# Revit family: Комби-клапан – регулятор расхода 4006_R_SMART_LF_MF
name_source: partatom
category: Rohrzubehör
revit_build: Autodesk Revit 2018 (Build: 20190510_1515(x64)
units: mm (PartAtom-declared; Revit-internal decimal feet)

## family parameters
Arbeitsebenenbasiert = Nein
Beim Laden mit Abzugskörper schneiden = Nein
Bemaßung runder Anschluss = Durchmesser verwenden
Gemeinsam genutzt = Nein
Immer vertikal = Ja
OmniClass-Nummer = 23.65.55.14
OmniClass-Titel = Valves for Liquid Services
Teiletyp = Unterbricht

## types (2) — shared parameters
B01 = 50 mm
B02 = 45.4 mm
B03 = 44.372 mm
B04 = 41.901 mm
B05 = 40.933 mm
B06 = 39.471 mm
B07 = 30.908 mm
B08 = 26 mm
B09 = 7.998 mm  [stored 0.0262402 ft]
E01 = 23 mm  [stored 0.0754593 ft]
E02 = 20.014 mm  [stored 0.0656627 ft]
E03 = 18.385 mm  [stored 0.0603182 ft]
E04 = 19.704 mm  [stored 0.0646457 ft]
E05 = 20.519 mm  [stored 0.0673196 ft]
E06 = 17.921 mm  [stored 0.0587959 ft]
E07 = 5.15 mm
E08 = 20.825 mm  [stored 0.0683235 ft]
E09 = 20.075 mm  [stored 0.0658629 ft]
E10 = 20.427 mm  [stored 0.0670177 ft]
E11 = 10.7 mm  [stored 0.035105 ft]
E12 = 9.001 mm
E13 = 11.063 mm  [stored 0.0362959 ft]
E14 = 20.506 mm  [stored 0.0672769 ft]
E15 = 21.877 mm  [stored 0.0717749 ft]
E16 = 23.7 mm  [stored 0.0777559 ft]
E17 = 28.85 mm
E18 = 5.15 mm
E19 = 5 mm  [stored 0.0164042 ft]
E20 = 108.221 mm
H03 = 6.351 mm  [stored 0.0208366 ft]
H04 = 12 mm  [stored 0.0393701 ft]
Hersteller = Herz-Armaturen GmbH
L01 = 41 mm
L02 = 34 mm
L03 = 28 mm
L04 = 21 mm  [stored 0.0688976 ft]
L05 = 9 mm  [stored 0.0295276 ft]
L06 = 7 mm  [stored 0.0229659 ft]
PN = 16
R02 = 4.67 mm  [stored 0.0153215 ft]
R03 = 5.755 mm  [stored 0.0188812 ft]
R04 = 7.193 mm  [stored 0.0235991 ft]
R05 = 12.954 mm  [stored 0.0425 ft]
R06 = 22 mm  [stored 0.0721785 ft]
R07 = 18.816 mm  [stored 0.0617323 ft]
R08 = 13.212 mm  [stored 0.0433465 ft]
R09 = 16.292 mm  [stored 0.0534514 ft]
R10 = 6.8 mm  [stored 0.0223097 ft]
R11 = 9.62 mm  [stored 0.0315617 ft]
R12 = 6.8 mm  [stored 0.0223097 ft]
R13 = 3.496 mm
R14 = 8.07 mm
R15 = 7.225 mm  [stored 0.0237041 ft]
S08 = 30 mm
S09 = 10 mm  [stored 0.0328084 ft]
SCRNCODE = 05;04;02
SCRNSEQ = ARM;ARM_TYP="DURR";2
URL = www.herz-armaturen.ru
V10 = 7 mm  [stored 0.0229659 ft]
V12 = 17 mm
VRL01 = 30 mm
Защитный колпачок = Пластик
Импульсная трубка = Медь Cu-DHP (CW024A)
Кольцевое уплотнение O-Ring = EPDM
Корпус = Латунь, устойчивая к селективной цинковой коррозии
Корпус мембраны = латунь CW602N
Макс. рабочая температура до DN32 = 130 °C
Макс. рабочая температура от DN40 = 110 °C
Макс. рабочее давление = 1600000.0 Pa
Мембрана = EPDM
Мин. рабочая температура (антифриз) = -20 °C
Мин. рабочая температура (чистая вода) = 2 °C
Область применения = Комби-клапан применяется в системах отопления и охлаждения с насосами. Комби-клапан автоматически ограничивает расход на выбранном участке системы до заданного значения, компенсируя все колебания давления. При этом нет необходимости в измерениях, а регулирование эффективно при любых условиях эксплуатации. Комби-клапан регулирует расход в соответствии с настройкой до заданного значения; на мембрану воздействует давление непосредственно до и после регулирующей части.
Пружина = Пружинная нержавеющая сталь
Среда = Качество теплоносителя в соответствии с ÖNORM H5195 и/или предписаниями VDI-Standard 2035.
Разрешается использование смеси этилен- или пропиленгликоля в соотношении 25-50% с водой.
Ход = 4 mm  [stored 0.0131234 ft]
Шпиндель = Нержавеющая сталь 14301

## type names (no varying parameters)
- LF
- MF

note: [stored X ft] marks values corroborated as IEEE doubles in the binary element streams (Revit-internal decimal feet)
